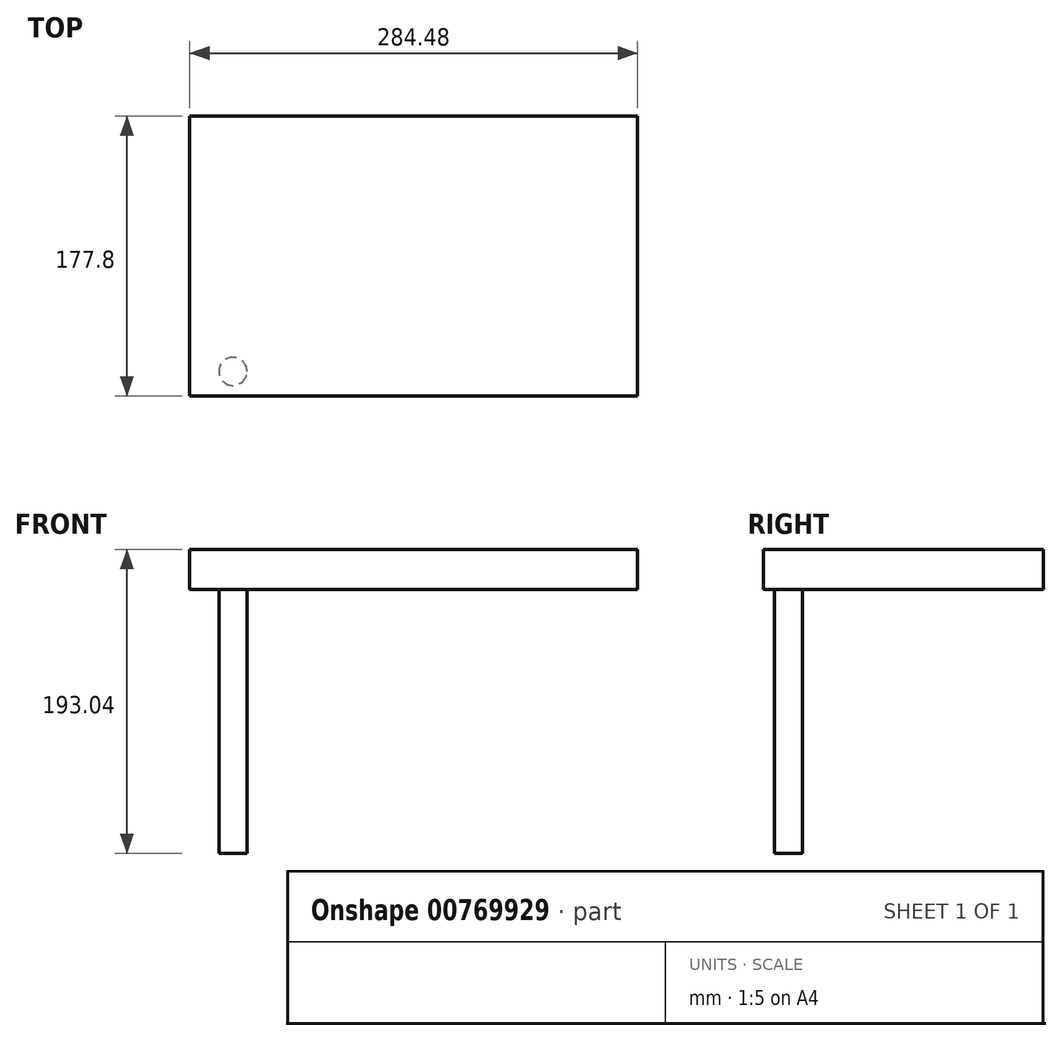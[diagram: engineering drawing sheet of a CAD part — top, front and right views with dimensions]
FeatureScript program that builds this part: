
annotation { "Feature Type Name" : "Feature", "Feature Type Description" : "" }
export const myFeature = defineFeature(function(context is Context, id is Id, definition is map)
    precondition{}
    {
        {
            var Q0;
            Q0=qCreatedBy(makeId("Top.planeOp"),FACE);
            var sketch = newSketch(context, id + "F0", { "sketchPlane" : qUnion([Q0])});
            skLineSegment(sketch, "E0.bottom", {"start": v(-150.66, -78.5) * mm, "end": v(133.82, -78.5) * mm});
            skLineSegment(sketch, "E0.top", {"start": v(-150.66, 99.3) * mm, "end": v(133.82, 99.3) * mm});
            skLineSegment(sketch, "E0.left", {"start": v(-150.66, -78.5) * mm, "end": v(-150.66, 99.3) * mm});
            skLineSegment(sketch, "E0.right", {"start": v(133.82, -78.5) * mm, "end": v(133.82, 99.3) * mm});
            skSolve(sketch);
        }
        {
            var Q0;
            Q0=makeQuery(id+"F0.imprint","IMPRINT",FACE,{"disambiguationData":[TD([[makeQuery(id+"F0.imprint","IMPRINT",EDGE,{"derivedFrom":sQuery(id+"F0.wireOp",EDGE,"E0.bottom")}),1.0]])]});
            extrude(context, id + "F1", {"entities" : qUnion([Q0]), "depth" : 25.4 * mm, "offsetDistance" : 25.4 * mm});
        }
        {
            var Q0;
            Q0=makeQuery(id+"F1.opExtrude","CAP_FACE",FACE,{"disambiguationData":[OSD([sQuery(id+"F0.wireOp",EDGE,"E0.bottom"),sQuery(id+"F0.wireOp",EDGE,"E0.top"),sQuery(id+"F0.wireOp",EDGE,"E0.left"),sQuery(id+"F0.wireOp",EDGE,"E0.right")])],"isStart":true});
            var sketch = newSketch(context, id + "F2", { "sketchPlane" : qUnion([Q0])});
            skPoint(sketch, "E1", {"position": v(-150.66, 78.5) * mm});
            skPoint(sketch, "E2", {"position": v(-150.66, -99.3) * mm});
            skPoint(sketch, "E3", {"position": v(133.82, 78.5) * mm});
            skPoint(sketch, "E4", {"position": v(133.82, -99.3) * mm});
            skPoint(sketch, "E5", {"position": v(0, 0) * mm});
            skPoint(sketch, "E6", {"position": v(-123.25, -71.46) * mm});
            skPoint(sketch, "E7", {"position": v(-123.25, 62.9) * mm});
            skPoint(sketch, "E8", {"position": v(121.33, 62.9) * mm});
            skPoint(sketch, "E9", {"position": v(121.33, -83.08) * mm});
            skCircle(sketch, "E10", {"center": v(-123.25, 62.9) * mm, "radius": 8.9 * mm});
            skCircle(sketch, "E11", {"center": v(-123.25, -71.46) * mm, "radius": 8.9 * mm});
            skCircle(sketch, "E12", {"center": v(121.33, 62.9) * mm, "radius": 8.9 * mm});
            skCircle(sketch, "E13", {"center": v(121.33, -83.08) * mm, "radius": 8.9 * mm});
            skSolve(sketch);
        }
        {
            var Q0;
            Q0=makeQuery(id+"F2.imprint","IMPRINT",FACE,{"disambiguationData":[TD([[makeQuery(id+"F2.imprint","IMPRINT",EDGE,{"derivedFrom":sQuery(id+"F2.wireOp",EDGE,"E10")}),1.0]])]});
            extrude(context, id + "F3", {"entities" : qUnion([Q0]), "operationType" : NewBodyOperationType.ADD, "depth" : 167.64 * mm, "offsetDistance" : 25.4 * mm});
        }
        {
            var Q0;
            Q0=sQuery(id+"F2.wireOp",EDGE,"E12");
            var Q1;
            Q1=sQuery(id+"F2.wireOp",EDGE,"E13");
            var Q2;
            Q2=sQuery(id+"F2.wireOp",EDGE,"E11");
            extrude(context, id + "F4", {"bodyType" : ToolBodyType.SURFACE, "surfaceEntities" : qUnion([Q0, Q1, Q2]), "depth" : 167.64 * mm, "offsetDistance" : 25.4 * mm});
        }
    });
